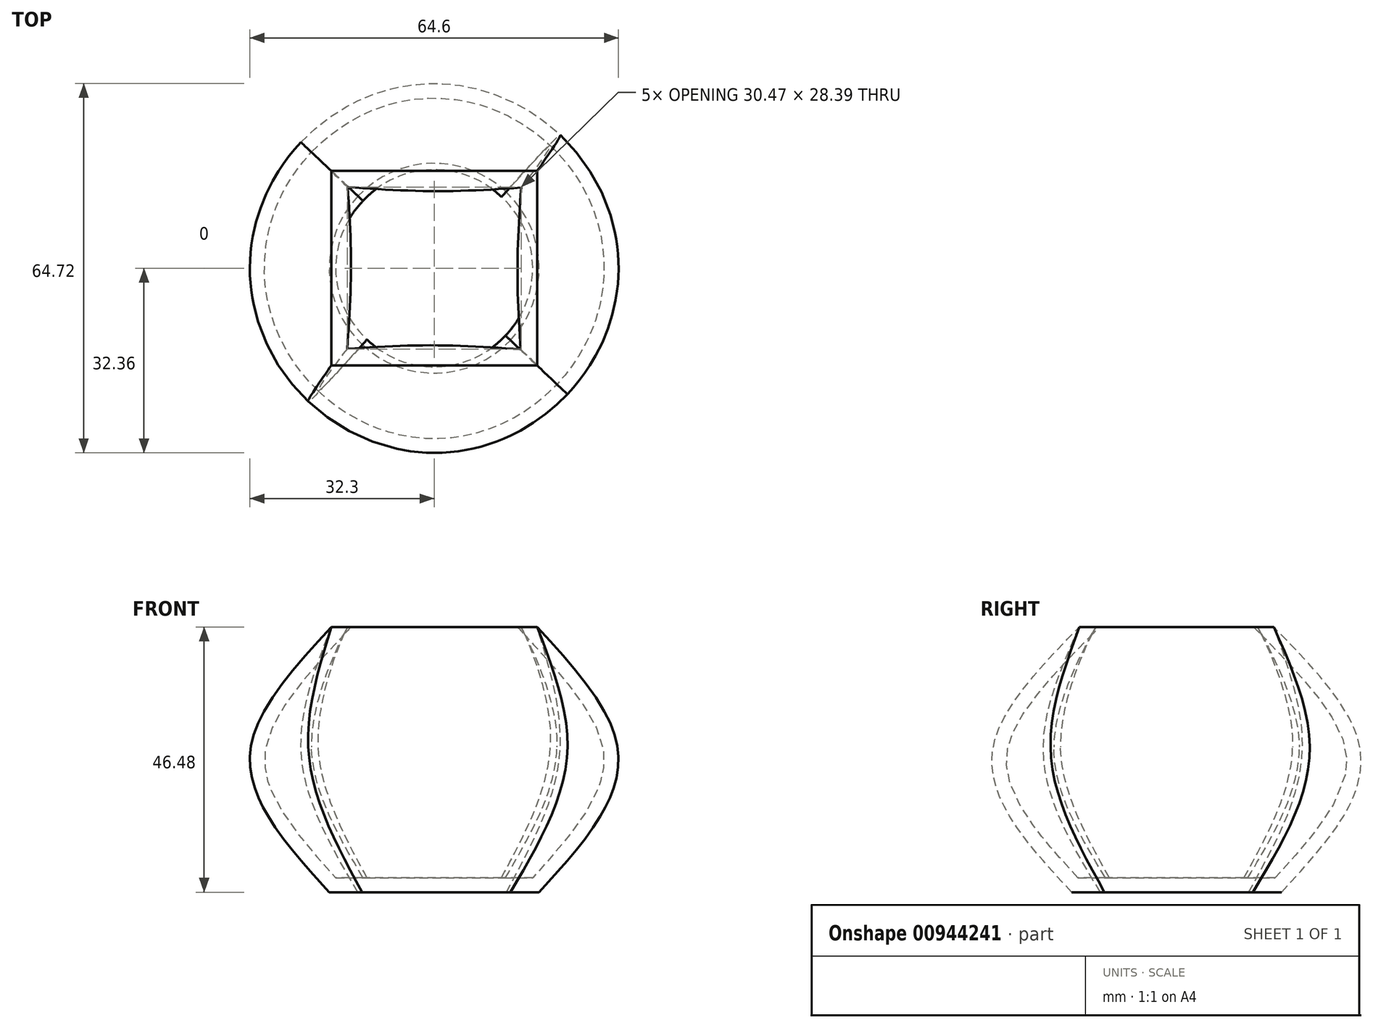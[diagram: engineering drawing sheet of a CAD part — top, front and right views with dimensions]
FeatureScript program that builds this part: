
annotation { "Feature Type Name" : "Feature", "Feature Type Description" : "" }
export const myFeature = defineFeature(function(context is Context, id is Id, definition is map)
    precondition{}
    {
        {
            var Q0;
            Q0=qCreatedBy(makeId("Top.planeOp"),FACE);
            var sketch = newSketch(context, id + "F0", { "sketchPlane" : qUnion([Q0])});
            skCircle(sketch, "E0", {"center": v(0, 0) * mm, "radius": 18.38 * mm});
            skSolve(sketch);
        }
        {
            var Q0;
            Q0=qCreatedBy(makeId("Top.planeOp"),FACE);
            cPlane(context, id + "F1", {"entities" : qUnion([Q0]), "cplaneType" : CPlaneType.OFFSET, "offset" : 46.48 * mm, "width" : 152.4 * mm, "height" : 152.4 * mm});
        }
        {
            var Q0;
            Q0=qCreatedBy(makeId("Top.planeOp"),FACE);
            cPlane(context, id + "F2", {"entities" : qUnion([Q0]), "cplaneType" : CPlaneType.OFFSET, "offset" : 25.4 * mm, "width" : 152.4 * mm, "height" : 152.4 * mm});
        }
        {
            var Q0;
            Q0=qCreatedBy(id+"F1.planeOp",FACE);
            var sketch = newSketch(context, id + "F3", { "sketchPlane" : qUnion([Q0])});
            skLineSegment(sketch, "E1.bottom", {"start": v(18.03, -17.05) * mm, "end": v(-18.03, -17.05) * mm});
            skLineSegment(sketch, "E1.top", {"start": v(18.03, 17.05) * mm, "end": v(-18.03, 17.05) * mm});
            skLineSegment(sketch, "E1.left", {"start": v(18.03, -17.05) * mm, "end": v(18.03, 17.05) * mm});
            skLineSegment(sketch, "E1.right", {"start": v(-18.03, -17.05) * mm, "end": v(-18.03, 17.05) * mm});
            skPoint(sketch, "E1.middle", {"position": v(0, 0) * mm});
            skSolve(sketch);
        }
        {
            var Q0;
            Q0=qCreatedBy(id+"F2.planeOp",FACE);
            var sketch = newSketch(context, id + "F4", { "sketchPlane" : qUnion([Q0])});
            skCircle(sketch, "E2", {"center": v(0, 0) * mm, "radius": 32.14 * mm});
            skSolve(sketch);
        }
        {
            var Q0;
            Q0=makeQuery(id+"F0.imprint","IMPRINT",FACE,{"disambiguationData":[TD([[makeQuery(id+"F0.imprint","IMPRINT",EDGE,{"derivedFrom":sQuery(id+"F0.wireOp",EDGE,"E0")}),1.0]])]});
            var Q1;
            Q1=makeQuery(id+"F4.imprint","IMPRINT",FACE,{"disambiguationData":[TD([[makeQuery(id+"F4.imprint","IMPRINT",EDGE,{"derivedFrom":sQuery(id+"F4.wireOp",EDGE,"E2")}),1.0]])]});
            var Q2;
            Q2=makeQuery(id+"F3.imprint","IMPRINT",FACE,{"disambiguationData":[TD([[makeQuery(id+"F3.imprint","IMPRINT",EDGE,{"derivedFrom":sQuery(id+"F3.wireOp",EDGE,"E1.bottom")}),-1.0]])]});
            loft(context, id + "F5", {"sheetProfilesArray" : [{ "sheetProfileEntities" : qUnion([Q0]) }, { "sheetProfileEntities" : qUnion([Q1]) }, { "sheetProfileEntities" : qUnion([Q2]) }]});
        }
        {
            var Q0;
            Q0=makeQuery(id+"F5.opLoft","CAP_FACE",FACE,{"disambiguationData":[OSD([makeQuery(id+"F3.imprint","IMPRINT",FACE,{"disambiguationData":[TD([[makeQuery(id+"F3.imprint","IMPRINT",EDGE,{"derivedFrom":sQuery(id+"F3.wireOp",EDGE,"E1.bottom")}),-1.0]])]})])],"isStart":true});
            shell(context, id + "F6", {"entities" : qUnion([Q0]), "thickness" : 2.54 * mm});
        }
    });
